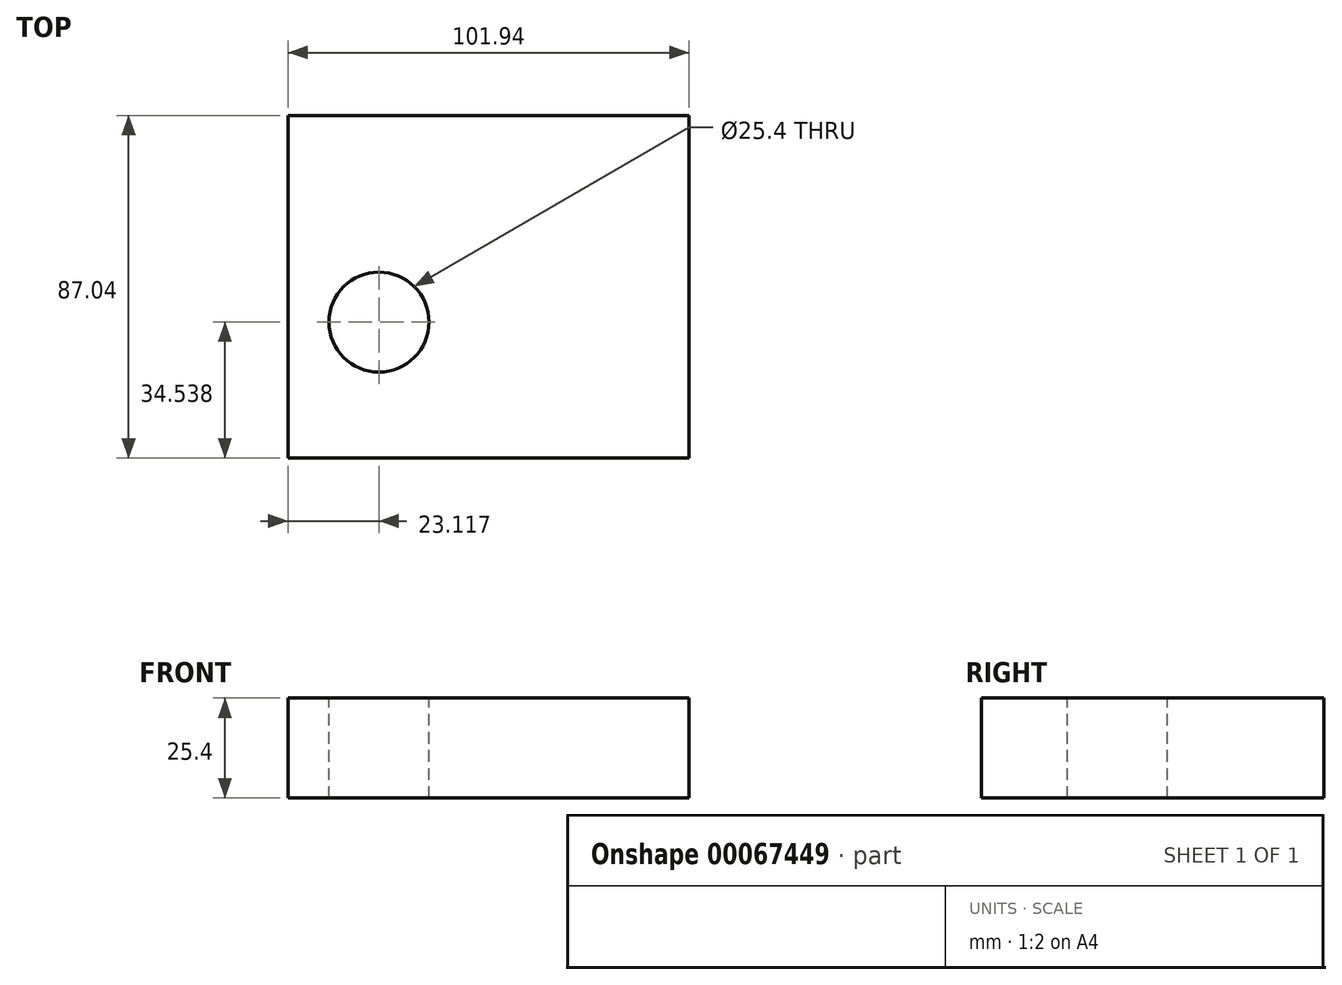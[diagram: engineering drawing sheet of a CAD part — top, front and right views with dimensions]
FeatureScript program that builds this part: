
annotation { "Feature Type Name" : "Feature", "Feature Type Description" : "" }
export const myFeature = defineFeature(function(context is Context, id is Id, definition is map)
    precondition{}
    {
        {
            var Q0;
            Q0=qCreatedBy(makeId("Top.planeOp"),FACE);
            var sketch = newSketch(context, id + "F0", { "sketchPlane" : qUnion([Q0])});
            skLineSegment(sketch, "E0.bottom", {"start": v(50.97, -43.52) * mm, "end": v(-50.97, -43.52) * mm});
            skLineSegment(sketch, "E0.top", {"start": v(50.97, 43.52) * mm, "end": v(-50.97, 43.52) * mm});
            skLineSegment(sketch, "E0.left", {"start": v(50.97, -43.52) * mm, "end": v(50.97, 43.52) * mm});
            skLineSegment(sketch, "E0.right", {"start": v(-50.97, -43.52) * mm, "end": v(-50.97, 43.52) * mm});
            skPoint(sketch, "E0.middle", {"position": v(0, 0) * mm});
            skSolve(sketch);
        }
        {
            var Q0;
            Q0=makeQuery(id+"F0.imprint","IMPRINT",FACE,{"disambiguationData":[TD([[makeQuery(id+"F0.imprint","IMPRINT",EDGE,{"derivedFrom":sQuery(id+"F0.wireOp",EDGE,"E0.bottom")}),-1.0]])]});
            extrude(context, id + "F1", {"entities" : qUnion([Q0]), "depth" : 25.4 * mm});
        }
        {
            var Q0;
            Q0=makeQuery(id+"F1.opExtrude","CAP_FACE",FACE,{"disambiguationData":[OSD([sQuery(id+"F0.wireOp",EDGE,"E0.bottom"),sQuery(id+"F0.wireOp",EDGE,"E0.top"),sQuery(id+"F0.wireOp",EDGE,"E0.left"),sQuery(id+"F0.wireOp",EDGE,"E0.right")])],"isStart":false});
            var sketch = newSketch(context, id + "F2", { "sketchPlane" : qUnion([Q0])});
            skCircle(sketch, "E1", {"center": v(-27.85, -8.98) * mm, "radius": 12.7 * mm});
            skSolve(sketch);
        }
        {
            var Q0;
            Q0=sQuery(id+"F2.wireOp",VERTEX,"E1.center");
            var Q1;
            Q1=makeQuery(id+"F1.opExtrude","SWEPT_BODY",BODY,{"disambiguationData":[OSD([sQuery(id+"F0.wireOp",EDGE,"E0.bottom"),sQuery(id+"F0.wireOp",EDGE,"E0.top"),sQuery(id+"F0.wireOp",EDGE,"E0.left"),sQuery(id+"F0.wireOp",EDGE,"E0.right")])]});
            hole(context, id + "F3", {"style" : HoleStyle.SIMPLE, "endStyle" : HoleEndStyle.THROUGH, "holeDiameter" : 25.4 * mm, "tappedDepth" : 12.7 * mm, "tapClearance" : 3, "locations" : qUnion([Q0]), "scope" : qUnion([Q1])});
        }
    });
